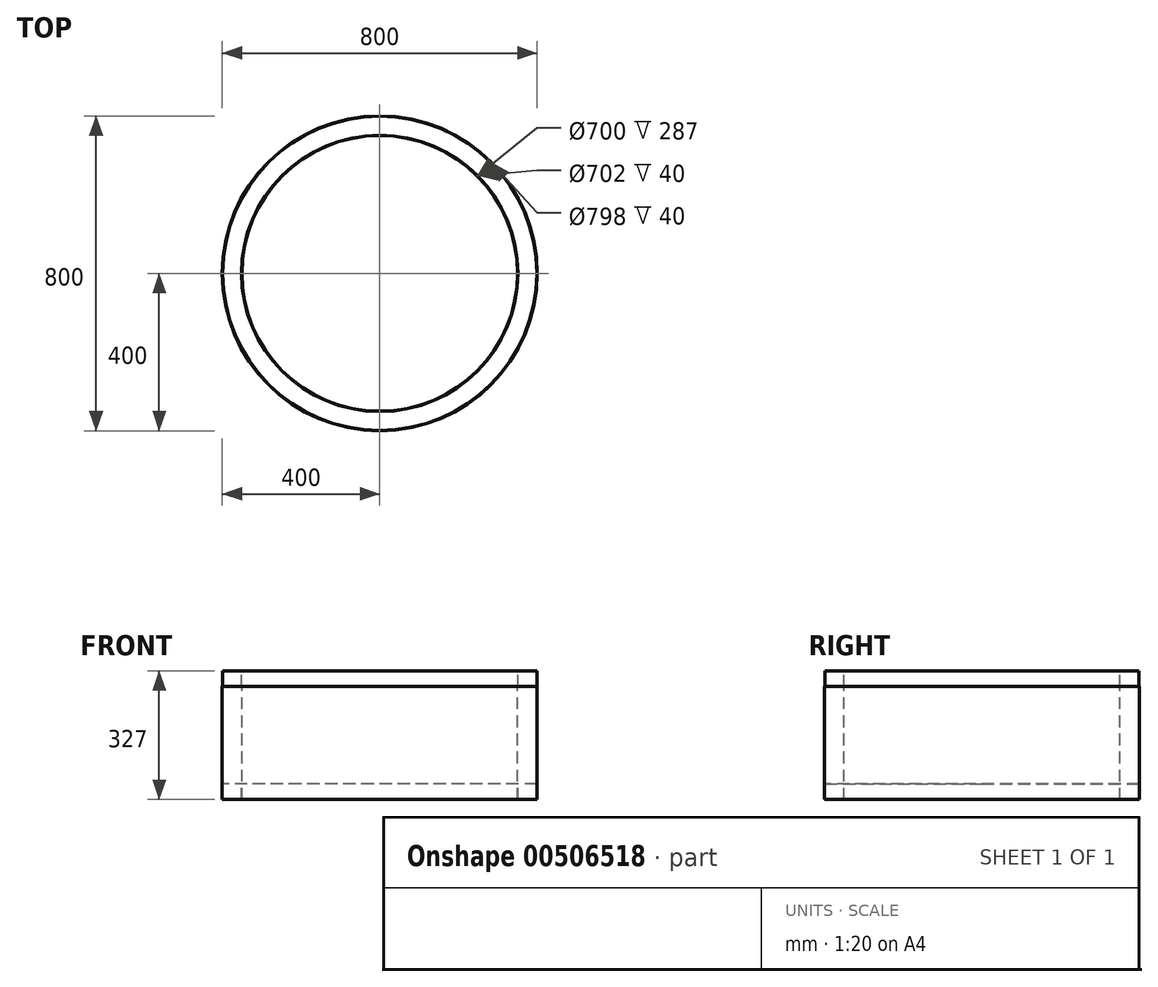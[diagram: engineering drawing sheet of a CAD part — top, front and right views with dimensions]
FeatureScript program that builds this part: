
annotation { "Feature Type Name" : "Feature", "Feature Type Description" : "" }
export const myFeature = defineFeature(function(context is Context, id is Id, definition is map)
    precondition{}
    {
        {
            var Q0;
            Q0=qCreatedBy(makeId("Front.planeOp"),FACE);
            var sketch = newSketch(context, id + "F0", { "sketchPlane" : qUnion([Q0])});
            skLineSegment(sketch, "E0", {"start": v(0, 74.87) * mm, "end": v(0, -73.71) * mm, "construction": true});
            skLineSegment(sketch, "E1", {"start": v(0, 374.84) * mm, "end": v(0, -528.94) * mm, "construction": true});
            skLineSegment(sketch, "E2", {"start": v(-350, -489.75) * mm, "end": v(-350, -202.75) * mm});
            skLineSegment(sketch, "E3", {"start": v(-350, -202.75) * mm, "end": v(-351, -202.75) * mm});
            skLineSegment(sketch, "E4", {"start": v(-351, -202.75) * mm, "end": v(-351, -162.75) * mm});
            skLineSegment(sketch, "E5", {"start": v(-351, -162.75) * mm, "end": v(-399, -162.75) * mm});
            skLineSegment(sketch, "E6", {"start": v(-399, -162.75) * mm, "end": v(-399, -202.75) * mm});
            skLineSegment(sketch, "E7", {"start": v(-399, -202.75) * mm, "end": v(-400, -202.75) * mm});
            skLineSegment(sketch, "E8", {"start": v(-400, -202.75) * mm, "end": v(-400, -489.75) * mm});
            skLineSegment(sketch, "E9", {"start": v(-400, -489.75) * mm, "end": v(-399, -489.75) * mm});
            skLineSegment(sketch, "E10", {"start": v(-399, -489.75) * mm, "end": v(-399, -449.75) * mm});
            skLineSegment(sketch, "E11", {"start": v(-399, -449.75) * mm, "end": v(-351, -449.75) * mm});
            skLineSegment(sketch, "E12", {"start": v(-351, -449.75) * mm, "end": v(-351, -489.75) * mm});
            skLineSegment(sketch, "E13", {"start": v(-351, -489.75) * mm, "end": v(-350, -489.75) * mm});
            skSolve(sketch);
        }
        {
            var Q0;
            Q0=qSketchRegion(id+"F0",true);
            var Q1;
            Q1=sQuery(id+"F0.wireOp",EDGE,"E1");
            revolve(context, id + "F1", {"entities" : qUnion([Q0]), "axis" : qUnion([Q1]), "revolveType" : RevolveType.FULL});
        }
    });
